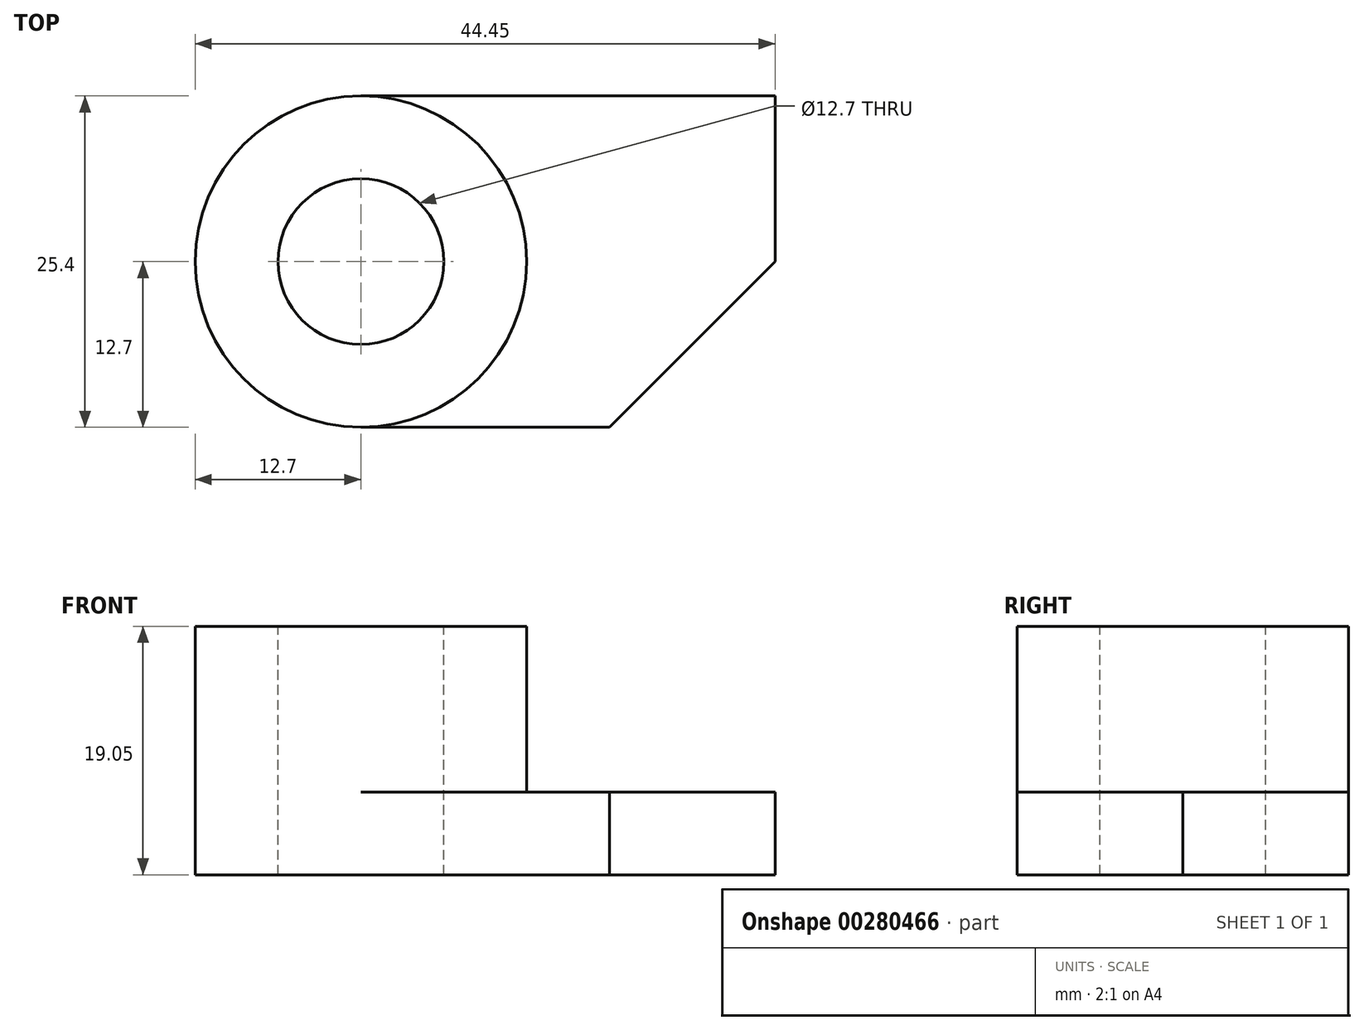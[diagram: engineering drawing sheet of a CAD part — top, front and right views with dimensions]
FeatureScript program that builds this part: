
annotation { "Feature Type Name" : "Feature", "Feature Type Description" : "" }
export const myFeature = defineFeature(function(context is Context, id is Id, definition is map)
    precondition{}
    {
        {
            var Q0;
            Q0=qCreatedBy(makeId("Top.planeOp"),FACE);
            var sketch = newSketch(context, id + "F0", { "sketchPlane" : qUnion([Q0])});
            skLineSegment(sketch, "E0.bottom", {"start": v(0, 0) * mm, "end": v(31.75, 0) * mm});
            skLineSegment(sketch, "E0.top", {"start": v(0, 25.4) * mm, "end": v(31.75, 25.4) * mm});
            skLineSegment(sketch, "E0.left", {"start": v(0, 0) * mm, "end": v(0, 25.4) * mm});
            skLineSegment(sketch, "E0.right", {"start": v(31.75, 0) * mm, "end": v(31.75, 25.4) * mm});
            skSolve(sketch);
        }
        {
            var Q0;
            Q0=makeQuery(id+"F0.imprint","IMPRINT",FACE,{"disambiguationData":[TD([[makeQuery(id+"F0.imprint","IMPRINT",EDGE,{"derivedFrom":sQuery(id+"F0.wireOp",EDGE,"E0.bottom")}),1.0]])]});
            extrude(context, id + "F1", {"entities" : qUnion([Q0]), "depth" : 6.35 * mm});
        }
        {
            var Q0;
            Q0=qCreatedBy(makeId("Top.planeOp"),FACE);
            var sketch = newSketch(context, id + "F2", { "sketchPlane" : qUnion([Q0])});
            skCircle(sketch, "E1", {"center": v(0, 12.7) * mm, "radius": 12.7 * mm});
            skSolve(sketch);
        }
        {
            var Q0;
            Q0 = qSketchRegion(id + "F2", true);
            extrude(context, id + "F3", {"entities" : qUnion([Q0]), "operationType" : NewBodyOperationType.ADD, "depth" : 19.05 * mm});
        }
        {
            var Q0;
            Q0=makeQuery(id+"F3.opExtrude","CAP_FACE",FACE,{"disambiguationData":[OSD([sQuery(id+"F2.wireOp",EDGE,"E1")])],"isStart":false});
            var sketch = newSketch(context, id + "F4", { "sketchPlane" : qUnion([Q0])});
            skCircle(sketch, "E2", {"center": v(0, 12.7) * mm, "radius": 6.35 * mm});
            skSolve(sketch);
        }
        {
            var Q0;
            Q0=makeQuery(id+"F4.imprint","IMPRINT",FACE,{"disambiguationData":[TD([[makeQuery(id+"F4.imprint","IMPRINT",EDGE,{"derivedFrom":sQuery(id+"F4.wireOp",EDGE,"E2")}),1.0]])]});
            extrude(context, id + "F5", {"entities" : qUnion([Q0]), "operationType" : NewBodyOperationType.REMOVE, "endBound" : BoundingType.THROUGH_ALL, "oppositeDirection" : true, "depth" : 25.4 * mm});
        }
        {
            var Q0;
            Q0=makeQuery(id+"F1.opExtrude","CAP_FACE",FACE,{"disambiguationData":[OSD([sQuery(id+"F0.wireOp",EDGE,"E0.bottom"),sQuery(id+"F0.wireOp",EDGE,"E0.top"),sQuery(id+"F0.wireOp",EDGE,"E0.left"),sQuery(id+"F0.wireOp",EDGE,"E0.right")])],"isStart":false});
            var sketch = newSketch(context, id + "F6", { "sketchPlane" : qUnion([Q0])});
            skLineSegment(sketch, "E3", {"start": v(31.75, 12.7) * mm, "end": v(19.05, 0) * mm});
            skLineSegment(sketch, "E4", {"start": v(19.05, 0) * mm, "end": v(31.75, 0) * mm});
            skLineSegment(sketch, "E5", {"start": v(31.75, 0) * mm, "end": v(31.75, 12.7) * mm});
            skSolve(sketch);
        }
        {
            var Q0;
            Q0 = qSketchRegion(id + "F6", true);
            extrude(context, id + "F7", {"entities" : qUnion([Q0]), "operationType" : NewBodyOperationType.REMOVE, "endBound" : BoundingType.THROUGH_ALL, "oppositeDirection" : true, "depth" : 25.4 * mm});
        }
    });
